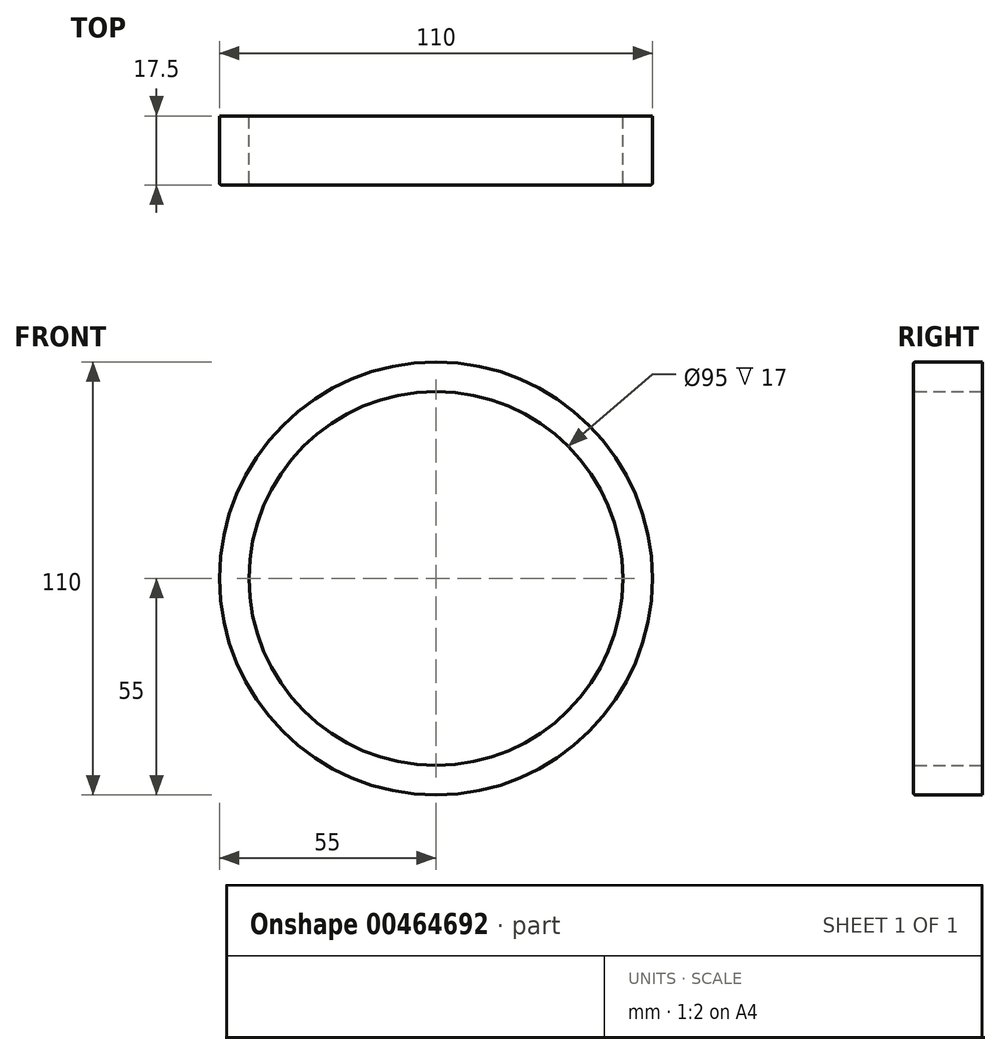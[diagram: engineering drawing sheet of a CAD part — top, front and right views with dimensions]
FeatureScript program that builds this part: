
annotation { "Feature Type Name" : "Feature", "Feature Type Description" : "" }
export const myFeature = defineFeature(function(context is Context, id is Id, definition is map)
    precondition{}
    {
        {
            var Q0;
            Q0=qCreatedBy(makeId("Front.planeOp"),FACE);
            var sketch = newSketch(context, id + "F0", { "sketchPlane" : qUnion([Q0])});
            skCircle(sketch, "E0", {"center": v(0, 0) * mm, "radius": 95 * mm, "construction": true});
            skCircle(sketch, "E1", {"center": v(0, 0) * mm, "radius": 105 * mm, "construction": true});
            skLineSegment(sketch, "E2", {"start": v(0, 0) * mm, "end": v(0, 105) * mm, "construction": true});
            skLineSegment(sketch, "E3.1.0", {"start": v(0, 0) * mm, "end": v(-67.5, 80.43) * mm, "construction": true});
            skLineSegment(sketch, "E3.2.0", {"start": v(0, 0) * mm, "end": v(-103.4, 18.23) * mm, "construction": true});
            skLineSegment(sketch, "E3.3.0", {"start": v(0, 0) * mm, "end": v(-90.93, -52.5) * mm, "construction": true});
            skLineSegment(sketch, "E3.4.0", {"start": v(0, 0) * mm, "end": v(-35.91, -98.67) * mm, "construction": true});
            skLineSegment(sketch, "E3.5.0", {"start": v(0, 0) * mm, "end": v(35.91, -98.67) * mm, "construction": true});
            skLineSegment(sketch, "E3.6.0", {"start": v(0, 0) * mm, "end": v(90.93, -52.5) * mm, "construction": true});
            skLineSegment(sketch, "E3.7.0", {"start": v(0, 0) * mm, "end": v(103.4, 18.23) * mm, "construction": true});
            skLineSegment(sketch, "E3.8.0", {"start": v(0, 0) * mm, "end": v(67.5, 80.43) * mm, "construction": true});
            skCircle(sketch, "E4", {"center": v(0, 0) * mm, "radius": 47.5 * mm});
            skCircle(sketch, "E5", {"center": v(0, 0) * mm, "radius": 55 * mm});
            skSolve(sketch);
        }
        {
            var Q0;
            Q0=makeQuery(id+"F0.imprint","IMPRINT",FACE,{"disambiguationData":[TD([[makeQuery(id+"F0.imprint","IMPRINT",EDGE,{"derivedFrom":sQuery(id+"F0.wireOp",EDGE,"E4")}),-1.0]])]});
            extrude(context, id + "F1", {"entities" : qUnion([Q0]), "depth" : 17.5 * mm});
        }
        {
            var Q0;
            Q0=makeQuery(id+"F1.opExtrude","CAP_EDGE",EDGE,{"disambiguationData":[OSD([sQuery(id+"F0.wireOp",EDGE,"E5")])],"isStart":false});
            fillet(context, id + "F2", {"entities" : qUnion([Q0]), "radius" : 0.5 * mm, "tangentPropagation" : true, "allowEdgeOverflow" : false});
        }
        {
            var Q0;
            Q0=makeQuery(id+"F1.opExtrude","CAP_EDGE",EDGE,{"disambiguationData":[OSD([sQuery(id+"F0.wireOp",EDGE,"E4")])],"isStart":false});
            fillet(context, id + "F3", {"entities" : qUnion([Q0]), "radius" : 0.5 * mm, "tangentPropagation" : true, "allowEdgeOverflow" : false});
        }
    });
